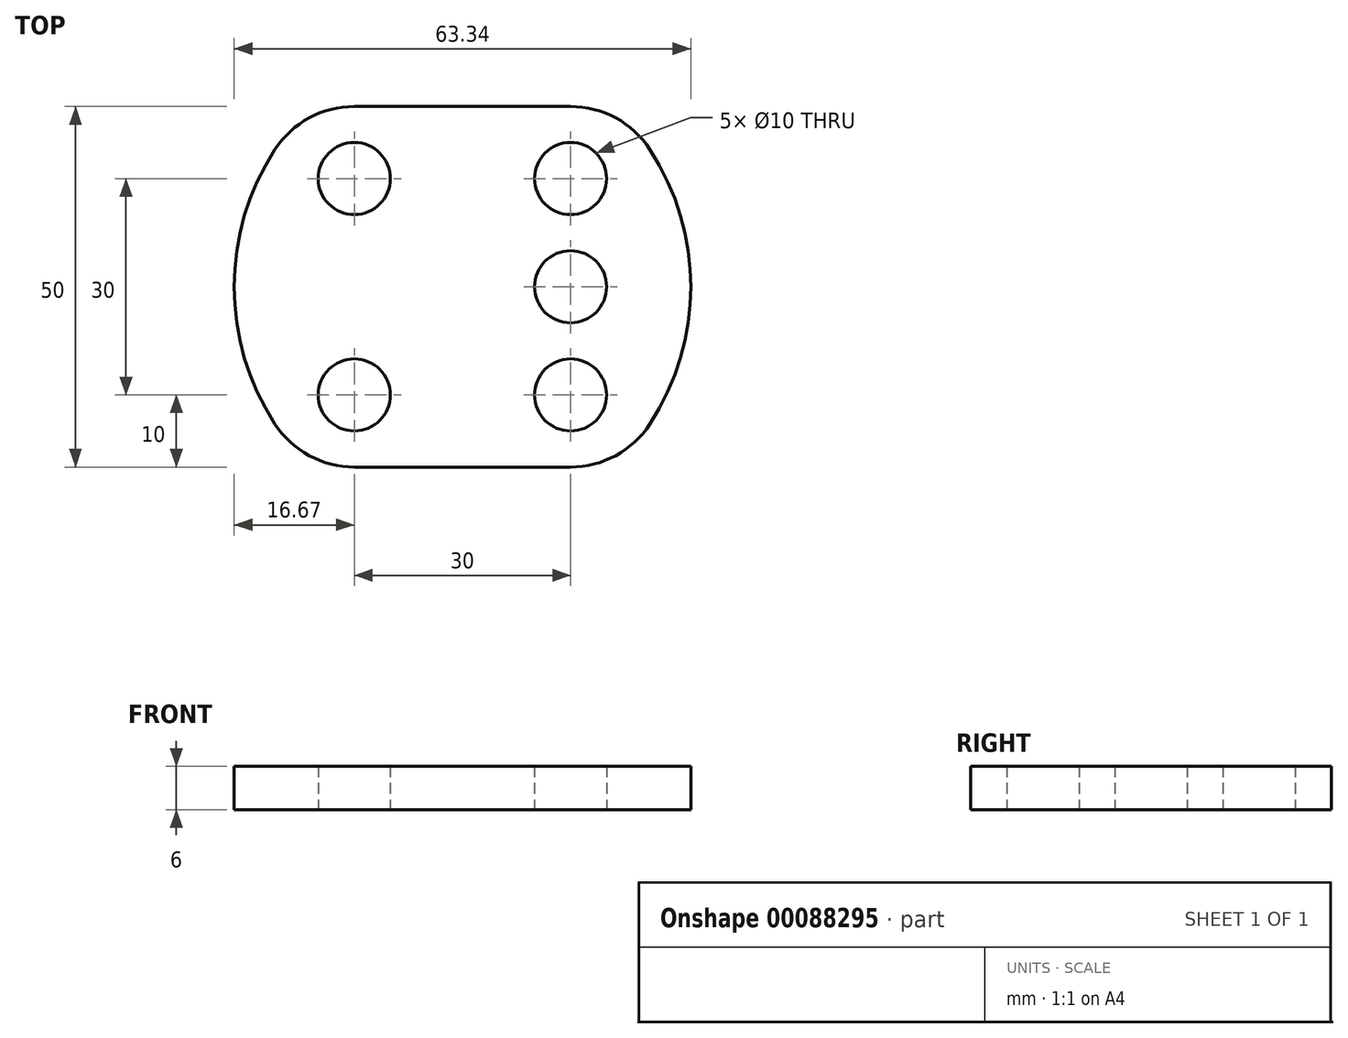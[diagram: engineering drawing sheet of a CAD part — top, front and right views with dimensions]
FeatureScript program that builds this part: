
annotation { "Feature Type Name" : "Feature", "Feature Type Description" : "" }
export const myFeature = defineFeature(function(context is Context, id is Id, definition is map)
    precondition{}
    {
        {
            var Q0;
            Q0=qCreatedBy(makeId("Top.planeOp"),FACE);
            var sketch = newSketch(context, id + "F0", { "sketchPlane" : qUnion([Q0])});
            skLineSegment(sketch, "E0.bottom", {"start": v(15, 25) * mm, "end": v(-15, 25) * mm});
            skLineSegment(sketch, "E0.top", {"start": v(15, -25) * mm, "end": v(-15, -25) * mm});
            skLineSegment(sketch, "E0.left", {"start": v(15, 25) * mm, "end": v(15, -25) * mm, "construction": true});
            skLineSegment(sketch, "E0.right", {"start": v(-15, 25) * mm, "end": v(-15, -25) * mm, "construction": true});
            skPoint(sketch, "E0.middle", {"position": v(0, 0) * mm});
            skArc(sketch, "E1", {"start": v(-15, 25) * mm, "mid": v(-40, 0) * mm, "end": v(-15, -25) * mm, "construction": true});
            skArc(sketch, "E2.MirrorCS", {"start": v(15, 25) * mm, "mid": v(40, 0) * mm, "end": v(15, -25) * mm, "construction": true});
            skCircle(sketch, "E3", {"center": v(-15, 15) * mm, "radius": 5 * mm});
            skCircle(sketch, "E4", {"center": v(-15, 0) * mm, "radius": 5 * mm, "construction": true});
            skCircle(sketch, "E5.MirrorC", {"center": v(-15, -15) * mm, "radius": 5 * mm});
            skCircle(sketch, "E6.MirrorC", {"center": v(15, -15) * mm, "radius": 5 * mm});
            skCircle(sketch, "E7.MirrorC", {"center": v(15, 0) * mm, "radius": 5 * mm});
            skCircle(sketch, "E8.MirrorC", {"center": v(15, 15) * mm, "radius": 5 * mm});
            skLineSegment(sketch, "E9", {"start": v(-15, 10) * mm, "end": v(-15, 5) * mm, "construction": true});
            skLineSegment(sketch, "E10", {"start": v(-15, 20) * mm, "end": v(-15, 25) * mm});
            skLineSegment(sketch, "E11.MirrorCS", {"start": v(-31.67, 0) * mm, "end": v(-40, 0) * mm, "construction": true});
            skLineSegment(sketch, "E12.MirrorCS", {"start": v(-15, 0) * mm, "end": v(-23.33, 0) * mm, "construction": true});
            skLineSegment(sketch, "E13.MirrorCS", {"start": v(-23.33, 0) * mm, "end": v(-31.67, 0) * mm, "construction": true});
            skLineSegment(sketch, "E14", {"start": v(-31.67, 0) * mm, "end": v(-31.67, 18.63) * mm, "construction": true});
            skArc(sketch, "E15", {"start": v(-26, 19.05) * mm, "mid": v(-30.22, 9.94) * mm, "end": v(-31.67, 0) * mm});
            skArc(sketch, "E16", {"start": v(-15, 25) * mm, "mid": v(-21.25, 23.42) * mm, "end": v(-26, 19.05) * mm});
            skLineSegment(sketch, "E17", {"start": v(-15, 0) * mm, "end": v(-27.5, 21.65) * mm, "construction": true});
            skArc(sketch, "E18.MirrorCS", {"start": v(-15, -25) * mm, "mid": v(-21.25, -23.42) * mm, "end": v(-26, -19.05) * mm});
            skArc(sketch, "E19.MirrorCS", {"start": v(-26, -19.05) * mm, "mid": v(-30.22, -9.94) * mm, "end": v(-31.67, 0) * mm});
            skCircle(sketch, "E20.MirrorC", {"center": v(15, 0) * mm, "radius": 5 * mm, "construction": true});
            skArc(sketch, "E21.MirrorCS", {"start": v(15, -25) * mm, "mid": v(21.25, -23.42) * mm, "end": v(26, -19.05) * mm});
            skArc(sketch, "E22.MirrorCS", {"start": v(26, -19.05) * mm, "mid": v(30.22, -9.94) * mm, "end": v(31.67, 0) * mm});
            skArc(sketch, "E23.MirrorCS", {"start": v(15, 25) * mm, "mid": v(21.25, 23.42) * mm, "end": v(26, 19.05) * mm});
            skArc(sketch, "E24.MirrorCS", {"start": v(26, 19.05) * mm, "mid": v(30.22, 9.94) * mm, "end": v(31.67, 0) * mm});
            skSolve(sketch);
        }
        {
            var Q0;
            Q0 = qSketchRegion(id + "F0", true);
            extrude(context, id + "F1", {"entities" : qUnion([Q0]), "depth" : 6 * mm});
        }
    });
